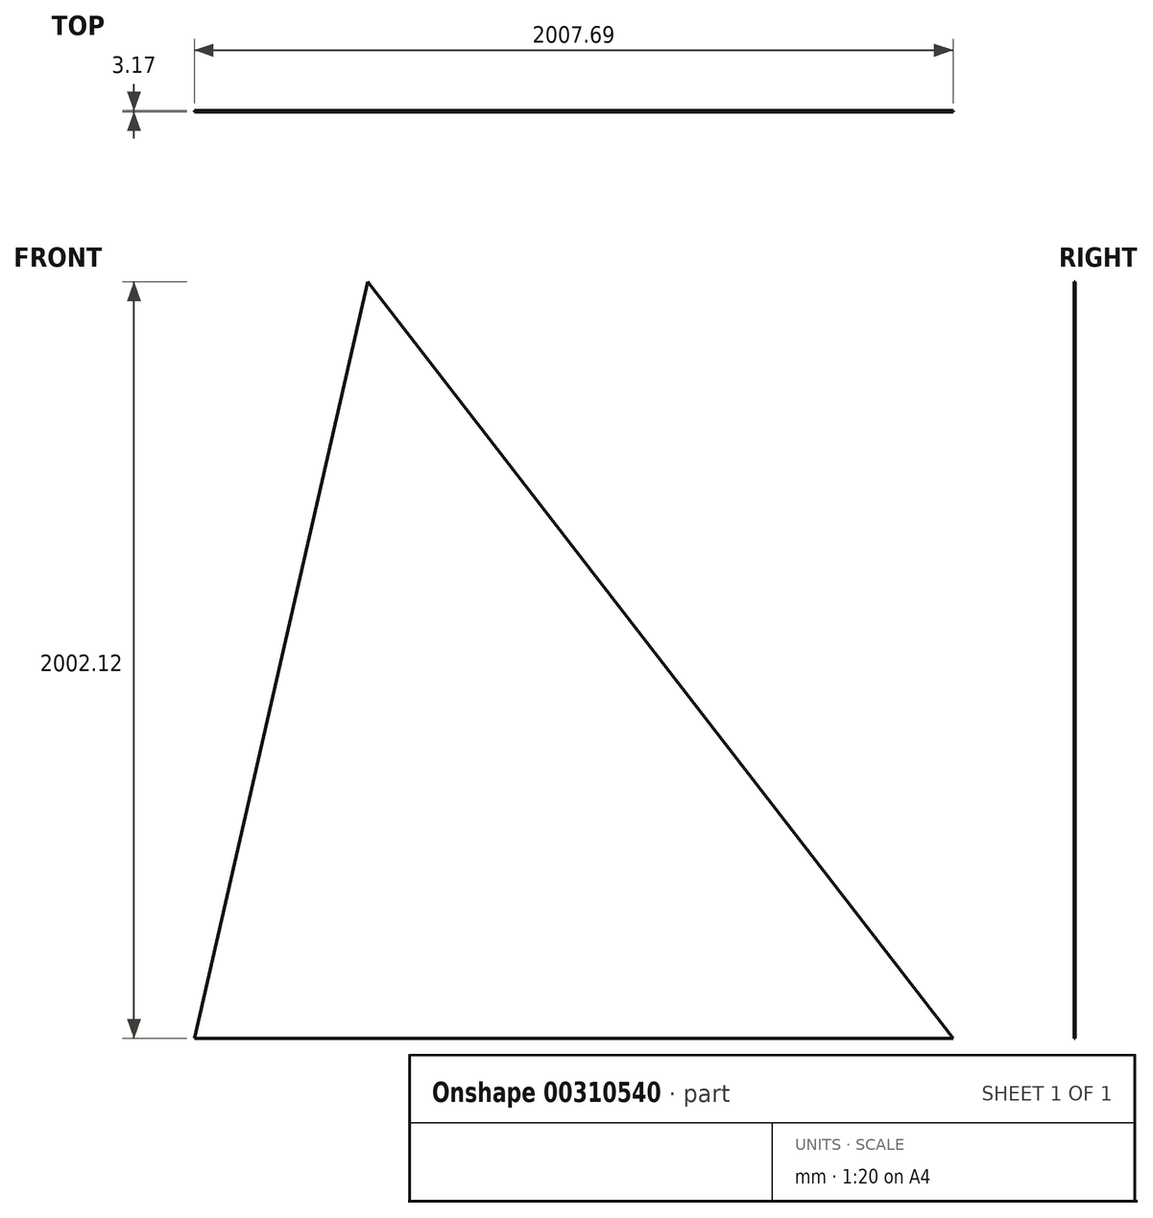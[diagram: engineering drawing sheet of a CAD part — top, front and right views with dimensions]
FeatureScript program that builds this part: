
annotation { "Feature Type Name" : "Feature", "Feature Type Description" : "" }
export const myFeature = defineFeature(function(context is Context, id is Id, definition is map)
    precondition{}
    {
        {
            var Q0;
            Q0=qCreatedBy(makeId("Front.planeOp"),FACE);
            var sketch = newSketch(context, id + "F0", { "sketchPlane" : qUnion([Q0])});
            skLineSegment(sketch, "E0.0", {"start": v(427.18, 1976.72) * mm, "end": v(1975.8, -25.4) * mm});
            skLineSegment(sketch, "E0.1", {"start": v(-31.88, -25.4) * mm, "end": v(427.18, 1976.72) * mm});
            skLineSegment(sketch, "E0.2", {"start": v(-31.88, -25.4) * mm, "end": v(1975.8, -25.4) * mm});
            skSolve(sketch);
        }
        {
            var Q0;
            Q0 = qSketchRegion(id + "F0", true);
            extrude(context, id + "F1", {"entities" : qUnion([Q0]), "depth" : 3.17 * mm});
        }
    });
